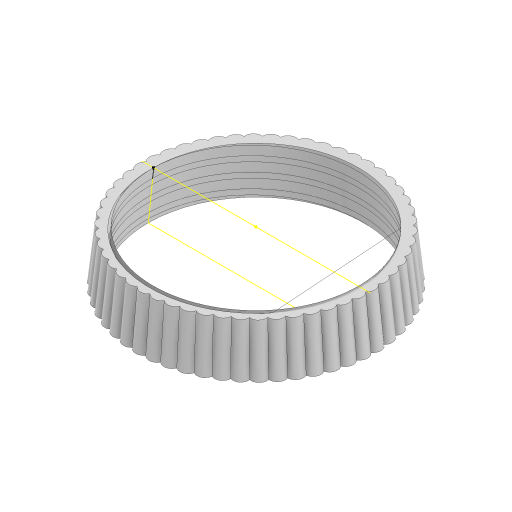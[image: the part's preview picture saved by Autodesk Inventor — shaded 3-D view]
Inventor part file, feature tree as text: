
AUTODESK INVENTOR PART (.ipt)
format: ipt  version: 2023 (Build 270158000, 158)  size: 438,784 bytes
history: native  units: mm
features: sketch x5, draft x2, helix x2, extrude x1, sweep x1, pattern_circular x1
ambient origin geometry x8: Origin, YZ Plane, XZ Plane, XY Plane, X Axis, Y Axis, Z Axis, Center Point
bodies: Solid1 (feature_tree)
feature tree (12):
  extrude  "Extrusion1"  Depth=6.52mm TaperAngle=0.0deg
  draft  "FaceDraft1"
  sketch  "Sketch2"  dims[d7=2.0mm d8=9.0mm d9=10.0mm d10=1.047198mm d11=90.0deg d12=90.0deg d13=0.0mm d14=0.0mm d15=2.0mm d16=3.0mm d17=10.0mm d18=-1.047198mm d19=90.0deg d20=90.0deg d21=0.0mm d22=0.0mm d23=1.5mm d91=1.047198mm]
  sketch  "Sketch4"  dims[d93=2.0mm d95=0.0mm d96=0.0mm d97=540.0mm d98=360.0deg]
  helix  "Coil1"  [1 undecoded]
  helix  "Coil2"  [1 undecoded]
  draft  "FaceDraft2"
  sweep  "Sweep1"
  pattern_circular  "Circular Pattern3"  Count=54 Angle=360.0deg
  sketch  "Sketch1"  dims[d0=26.5mm d2=6.52mm d3=0.0mm d4=1.047198mm]
  sketch  "Sketch9"
  sketch  "Sketch10"
note: 2 required parameter values undecoded (feature->parameter linkage not recoverable at this tier; creation-order binding heuristic only, values carry confidence <= 0.55)
